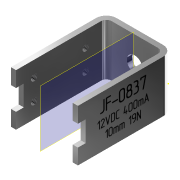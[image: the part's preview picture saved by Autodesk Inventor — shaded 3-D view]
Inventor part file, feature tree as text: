
AUTODESK INVENTOR PART (.ipt)
format: ipt  version: 2018.1 (Build 221171000, 171)  size: 171,008 bytes
history: native  units: mm
features: other x7, hole x4, sketch x3, imported_body x1, mirror x1
ambient origin geometry x8: Origin, YZ Plane, XZ Plane, XY Plane, X Axis, Y Axis, Z Axis, Center Point
bodies: Body1 (feature_tree)
feature tree (16):
  imported_body  "base"
  other  "Твердое тело1"
  other  "Грань1"
  other  "Грань3"
  other  "РабПлоскость3"
  mirror  "Зеркальное отражение2"
  hole  "Отверстие1"  [1 undecoded]
  hole  "Отверстие2"  [1 undecoded]
  hole  "Отверстие3"  [1 undecoded]
  hole  "Отверстие4"  [1 undecoded]
  sketch  "Эскиз3"
  sketch  "Эскиз1"
  other  "Пластина1"
  sketch  "Эскиз2"
  other  "Пластина3"
  other  "Сгиб2"
note: 4 required parameter values undecoded (feature->parameter linkage not recoverable at this tier; creation-order binding heuristic only, values carry confidence <= 0.55)
